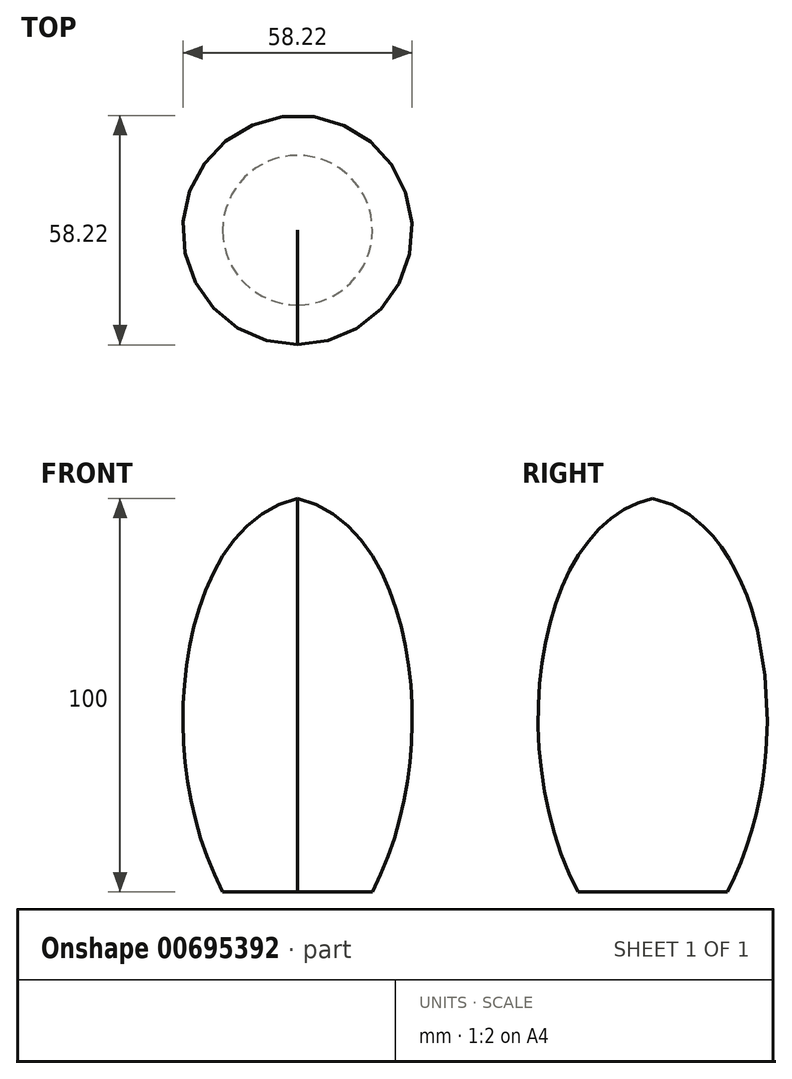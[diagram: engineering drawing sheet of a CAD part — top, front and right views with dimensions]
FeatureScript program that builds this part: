
annotation { "Feature Type Name" : "Feature", "Feature Type Description" : "" }
export const myFeature = defineFeature(function(context is Context, id is Id, definition is map)
    precondition{}
    {
        {
            var Q0;
            Q0=qCreatedBy(makeId("Right.planeOp"),FACE);
            var sketch = newSketch(context, id + "F0", { "sketchPlane" : qUnion([Q0])});
            skLineSegment(sketch, "E0", {"start": v(0, -43.55) * mm, "end": v(-19, -43.55) * mm});
            skLineSegment(sketch, "E1", {"start": v(0, -43.55) * mm, "end": v(0, 56.45) * mm});
            skFitSpline(sketch, "E2", {"points": [v(0, 56.45) * mm, v(-19, -43.55) * mm], "startDerivative": vector(-90.07, -20.53) * mm, "endDerivative": vector(55.95, -106.5) * mm});
            skSolve(sketch);
        }
        {
            var Q0;
            Q0 = qSketchRegion(id + "F0", true);
            var Q1;
            Q1=sQuery(id+"F0.wireOp",EDGE,"E1");
            revolve(context, id + "F1", {"entities" : qUnion([Q0]), "axis" : qUnion([Q1]), "revolveType" : RevolveType.FULL});
        }
    });
